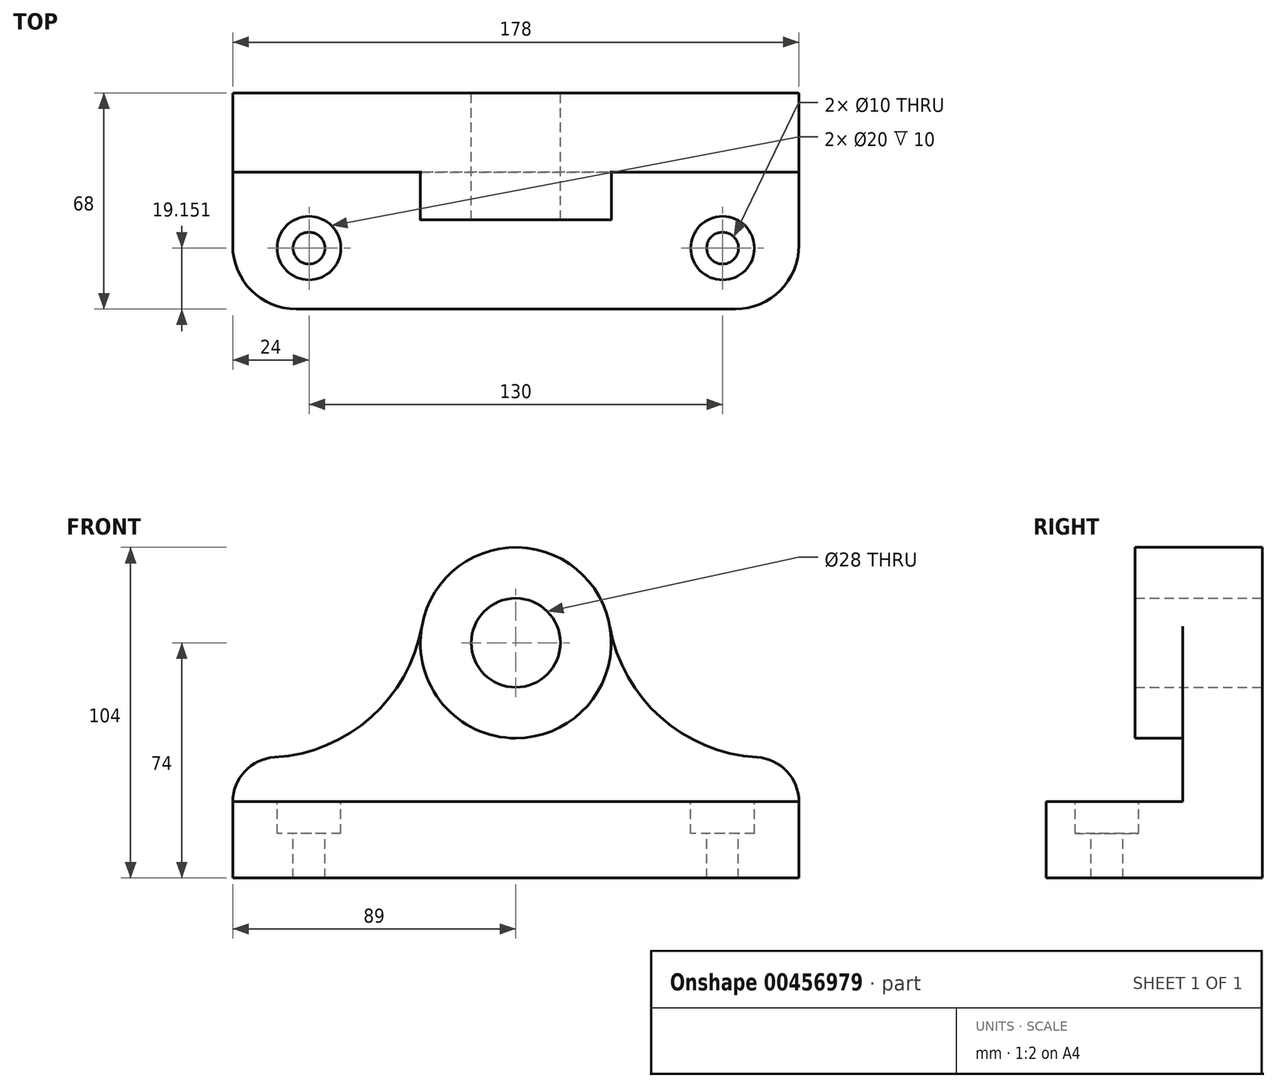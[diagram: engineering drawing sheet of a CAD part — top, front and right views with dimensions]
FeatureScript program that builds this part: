
annotation { "Feature Type Name" : "Feature", "Feature Type Description" : "" }
export const myFeature = defineFeature(function(context is Context, id is Id, definition is map)
    precondition{}
    {
        {
            var Q0;
            Q0=qCreatedBy(makeId("Front.planeOp"),FACE);
            var sketch = newSketch(context, id + "F0", { "sketchPlane" : qUnion([Q0])});
            skCircle(sketch, "E0", {"center": v(0, 0) * mm, "radius": 30 * mm});
            skArc(sketch, "E1", {"start": v(-75.83, -36.02) * mm, "mid": v(-45.53, -23.45) * mm, "end": v(-29.54, 5.2) * mm});
            skArc(sketch, "E2", {"start": v(29.54, 5.2) * mm, "mid": v(45.53, -23.45) * mm, "end": v(75.83, -36.02) * mm});
            skArc(sketch, "E3", {"start": v(-75.83, -36.02) * mm, "mid": v(-85.19, -40.4) * mm, "end": v(-89, -50) * mm});
            skArc(sketch, "E4", {"start": v(89, -50) * mm, "mid": v(85.19, -40.4) * mm, "end": v(75.83, -36.02) * mm});
            skLineSegment(sketch, "E5.bottom", {"start": v(-89, -50) * mm, "end": v(89, -50) * mm});
            skLineSegment(sketch, "E5.top", {"start": v(-89, -74) * mm, "end": v(89, -74) * mm});
            skLineSegment(sketch, "E5.left", {"start": v(-89, -50) * mm, "end": v(-89, -74) * mm});
            skLineSegment(sketch, "E5.right", {"start": v(89, -50) * mm, "end": v(89, -74) * mm});
            skLineSegment(sketch, "E6", {"start": v(0, -6.24) * mm, "end": v(0, -50) * mm, "construction": true});
            skCircle(sketch, "E7", {"center": v(0, 0) * mm, "radius": 14 * mm});
            skSolve(sketch);
        }
        {
            var Q0;
            Q0 = qSketchRegion(id + "F0", true);
            extrude(context, id + "F1", {"entities" : qUnion([Q0]), "depth" : 25 * mm});
        }
        {
            var Q0;
            Q0=makeQuery(id+"F0.imprint","IMPRINT",FACE,{"disambiguationData":[TD([[makeQuery(id+"F0.imprint","IMPRINT",EDGE,{"derivedFrom":sQuery(id+"F0.wireOp",EDGE,"E7")}),-1.0]])]});
            extrude(context, id + "F2", {"entities" : qUnion([Q0]), "operationType" : NewBodyOperationType.ADD, "depth" : 40 * mm});
        }
        {
            var Q0;
            Q0=makeQuery(id+"F0.imprint","IMPRINT",FACE,{"disambiguationData":[TD([[makeQuery(id+"F0.imprint","IMPRINT",EDGE,{"derivedFrom":sQuery(id+"F0.wireOp",EDGE,"E5.bottom")}),-1.0]])]});
            extrude(context, id + "F3", {"entities" : qUnion([Q0]), "operationType" : NewBodyOperationType.ADD, "depth" : 68 * mm});
        }
        {
            var Q0;
            Q0=makeQuery(id+"F3.opExtrude","CAP_EDGE",EDGE,{"disambiguationData":[OSD([sQuery(id+"F0.wireOp",EDGE,"E5.left")])],"isStart":false});
            var Q1;
            Q1=makeQuery(id+"F3.opExtrude","CAP_EDGE",EDGE,{"disambiguationData":[OSD([sQuery(id+"F0.wireOp",EDGE,"E5.right")])],"isStart":false});
            fillet(context, id + "F4", {"entities" : qUnion([Q0, Q1]), "radius" : 20 * mm, "tangentPropagation" : true, "allowEdgeOverflow" : false});
        }
        {
            var Q0;
            Q0=makeQuery(id+"F3.opExtrude","SWEPT_FACE",FACE,{"disambiguationData":[OSD([sQuery(id+"F0.wireOp",EDGE,"E5.bottom")])]});
            var sketch = newSketch(context, id + "F5", { "sketchPlane" : qUnion([Q0])});
            skPoint(sketch, "E8", {"position": v(-65, -48.85) * mm});
            skPoint(sketch, "E9", {"position": v(65, -48.85) * mm});
            skPoint(sketch, "E10.endSnap0", {"position": v(0, -25) * mm});
            skSolve(sketch);
        }
        {
            var Q0;
            Q0=sQuery(id+"F5.wireOp",VERTEX,"E8");
            var Q1;
            Q1=sQuery(id+"F5.wireOp",VERTEX,"E9");
            var Q2;
            Q2=makeQuery(id+"F1.opExtrude","SWEPT_BODY",BODY,{"disambiguationData":[OSD([sQuery(id+"F0.wireOp",EDGE,"E0"),sQuery(id+"F0.wireOp",EDGE,"E1"),sQuery(id+"F0.wireOp",EDGE,"E2"),sQuery(id+"F0.wireOp",EDGE,"E3"),sQuery(id+"F0.wireOp",EDGE,"E4"),sQuery(id+"F0.wireOp",EDGE,"E5.top"),sQuery(id+"F0.wireOp",EDGE,"E5.left"),sQuery(id+"F0.wireOp",EDGE,"E5.right"),sQuery(id+"F0.wireOp",EDGE,"E7")])]});
            hole(context, id + "F6", {"style" : HoleStyle.C_BORE, "endStyle" : HoleEndStyle.THROUGH, "holeDiameter" : 10 * mm, "cBoreDiameter" : 20 * mm, "cBoreDepth" : 10 * mm, "isTappedThrough" : true, "tappedDepth" : 12 * mm, "tapClearance" : 3, "locations" : qUnion([Q0, Q1]), "scope" : qUnion([Q2])});
        }
    });
